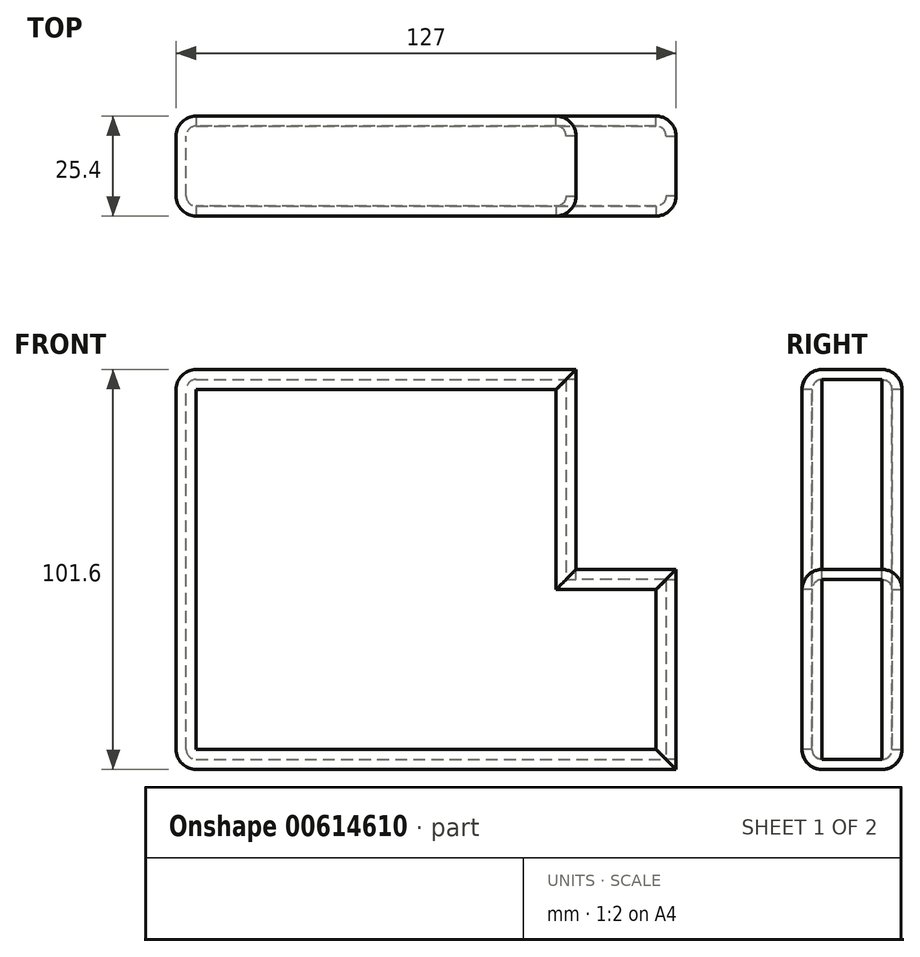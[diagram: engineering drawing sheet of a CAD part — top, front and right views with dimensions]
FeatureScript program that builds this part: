
annotation { "Feature Type Name" : "Feature", "Feature Type Description" : "" }
export const myFeature = defineFeature(function(context is Context, id is Id, definition is map)
    precondition{}
    {
        {
            var Q0;
            Q0=qCreatedBy(makeId("Front.planeOp"),FACE);
            var sketch = newSketch(context, id + "F0", { "sketchPlane" : qUnion([Q0])});
            skLineSegment(sketch, "E0", {"start": v(-63.6, -101.6) * mm, "end": v(63.4, -101.6) * mm});
            skLineSegment(sketch, "E1", {"start": v(63.4, -50.8) * mm, "end": v(63.4, -101.6) * mm});
            skLineSegment(sketch, "E2", {"start": v(63.4, -50.8) * mm, "end": v(38, -50.8) * mm});
            skLineSegment(sketch, "E3", {"start": v(38, -50.8) * mm, "end": v(38, 0) * mm});
            skLineSegment(sketch, "E4", {"start": v(-63.6, -101.6) * mm, "end": v(-63.6, 0) * mm});
            skLineSegment(sketch, "E5", {"start": v(-63.6, 0) * mm, "end": v(38, 0) * mm});
            skSolve(sketch);
        }
        {
            var Q0;
            Q0=makeQuery(id+"F0.imprint","IMPRINT",FACE,{"disambiguationData":[TD([[makeQuery(id+"F0.imprint","IMPRINT",EDGE,{"derivedFrom":sQuery(id+"F0.wireOp",EDGE,"E0")}),1.0]])]});
            extrude(context, id + "F1", {"entities" : qUnion([Q0]), "depth" : 25.4 * mm, "offsetDistance" : 25.4 * mm});
        }
        {
            var Q0;
            Q0=makeQuery(id+"F1.opExtrude","CAP_EDGE",EDGE,{"disambiguationData":[OSD([sQuery(id+"F0.wireOp",EDGE,"E0")])],"isStart":false});
            var Q1;
            Q1=makeQuery(id+"F1.opExtrude","CAP_EDGE",EDGE,{"disambiguationData":[OSD([sQuery(id+"F0.wireOp",EDGE,"E1")])],"isStart":false});
            var Q2;
            Q2=makeQuery(id+"F1.opExtrude","CAP_EDGE",EDGE,{"disambiguationData":[OSD([sQuery(id+"F0.wireOp",EDGE,"E2")])],"isStart":false});
            var Q3;
            Q3=makeQuery(id+"F1.opExtrude","CAP_EDGE",EDGE,{"disambiguationData":[OSD([sQuery(id+"F0.wireOp",EDGE,"E3")])],"isStart":false});
            var Q4;
            Q4=makeQuery(id+"F1.opExtrude","CAP_EDGE",EDGE,{"disambiguationData":[OSD([sQuery(id+"F0.wireOp",EDGE,"E5")])],"isStart":false});
            var Q5;
            Q5=makeQuery(id+"F1.opExtrude","CAP_EDGE",EDGE,{"disambiguationData":[OSD([sQuery(id+"F0.wireOp",EDGE,"E4")])],"isStart":false});
            var Q6;
            Q6=makeQuery(id+"F1.opExtrude","CAP_EDGE",EDGE,{"disambiguationData":[OSD([sQuery(id+"F0.wireOp",EDGE,"E4")])],"isStart":true});
            var Q7;
            Q7=makeQuery(id+"F1.opExtrude","SWEPT_EDGE",EDGE,{"disambiguationData":[OSD([sQuery(id+"F0.wireOp",EDGE,"E0"),sQuery(id+"F0.wireOp",EDGE,"E4")])]});
            var Q8;
            Q8=makeQuery(id+"F1.opExtrude","CAP_EDGE",EDGE,{"disambiguationData":[OSD([sQuery(id+"F0.wireOp",EDGE,"E0")])],"isStart":true});
            var Q9;
            Q9=makeQuery(id+"F1.opExtrude","CAP_EDGE",EDGE,{"disambiguationData":[OSD([sQuery(id+"F0.wireOp",EDGE,"E2")])],"isStart":true});
            var Q10;
            Q10=makeQuery(id+"F1.opExtrude","CAP_EDGE",EDGE,{"disambiguationData":[OSD([sQuery(id+"F0.wireOp",EDGE,"E3")])],"isStart":true});
            var Q11;
            Q11=makeQuery(id+"F1.opExtrude","CAP_EDGE",EDGE,{"disambiguationData":[OSD([sQuery(id+"F0.wireOp",EDGE,"E5")])],"isStart":true});
            var Q12;
            Q12=makeQuery(id+"F1.opExtrude","SWEPT_EDGE",EDGE,{"disambiguationData":[OSD([sQuery(id+"F0.wireOp",EDGE,"E4"),sQuery(id+"F0.wireOp",EDGE,"E5")])]});
            var Q13;
            Q13=makeQuery(id+"F1.opExtrude","CAP_EDGE",EDGE,{"disambiguationData":[OSD([sQuery(id+"F0.wireOp",EDGE,"E1")])],"isStart":true});
            fillet(context, id + "F2", {"entities" : qUnion([Q0, Q1, Q2, Q3, Q4, Q5, Q6, Q7, Q8, Q9, Q10, Q11, Q12, Q13]), "radius" : 5.08 * mm, "tangentPropagation" : true, "allowEdgeOverflow" : false});
        }
        {
            var Q0;
            Q0=makeQuery(id+"F1.opExtrude","SWEPT_FACE",FACE,{"disambiguationData":[OSD([sQuery(id+"F0.wireOp",EDGE,"E3")])]});
            var Q1;
            Q1=makeQuery(id+"F1.opExtrude","SWEPT_FACE",FACE,{"disambiguationData":[OSD([sQuery(id+"F0.wireOp",EDGE,"E1")])]});
            var Q2;
            Q2=makeQuery(id+"F1.opExtrude","CAP_FACE",FACE,{"disambiguationData":[OSD([sQuery(id+"F0.wireOp",EDGE,"E0"),sQuery(id+"F0.wireOp",EDGE,"E1"),sQuery(id+"F0.wireOp",EDGE,"E2"),sQuery(id+"F0.wireOp",EDGE,"E3"),sQuery(id+"F0.wireOp",EDGE,"E4"),sQuery(id+"F0.wireOp",EDGE,"E5")])],"isStart":true});
            var Q3;
            Q3=makeQuery(id+"F1.opExtrude","CAP_FACE",FACE,{"disambiguationData":[OSD([sQuery(id+"F0.wireOp",EDGE,"E0"),sQuery(id+"F0.wireOp",EDGE,"E1"),sQuery(id+"F0.wireOp",EDGE,"E2"),sQuery(id+"F0.wireOp",EDGE,"E3"),sQuery(id+"F0.wireOp",EDGE,"E4"),sQuery(id+"F0.wireOp",EDGE,"E5")])],"isStart":false});
            shell(context, id + "F3", {"entities" : qUnion([Q0, Q1, Q2, Q3]), "thickness" : 2.54 * mm});
        }
    });
